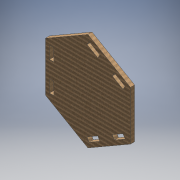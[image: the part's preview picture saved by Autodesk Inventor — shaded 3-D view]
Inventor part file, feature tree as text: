
AUTODESK INVENTOR PART (.ipt)
format: ipt  version: 2016 (Build 200138000, 138)  size: 166,400 bytes
history: native  units: mm
features: extrude x1, sketch x1
ambient origin geometry x8: Origin, YZ Plane, XZ Plane, XY Plane, X Axis, Y Axis, Z Axis, Center Point
bodies: Solid1 (feature_tree)
feature tree (2):
  extrude  "Extrusion1"  Depth=6.39mm
  sketch  "Sketch1"  dims[d0=60.0mm d2=150.0mm d3=6.3261mm d4=18.958829mm d5=6.39mm d6=12.78mm d7=30.0mm d9=360.0deg d11=6.39mm d12=0.0mm]
